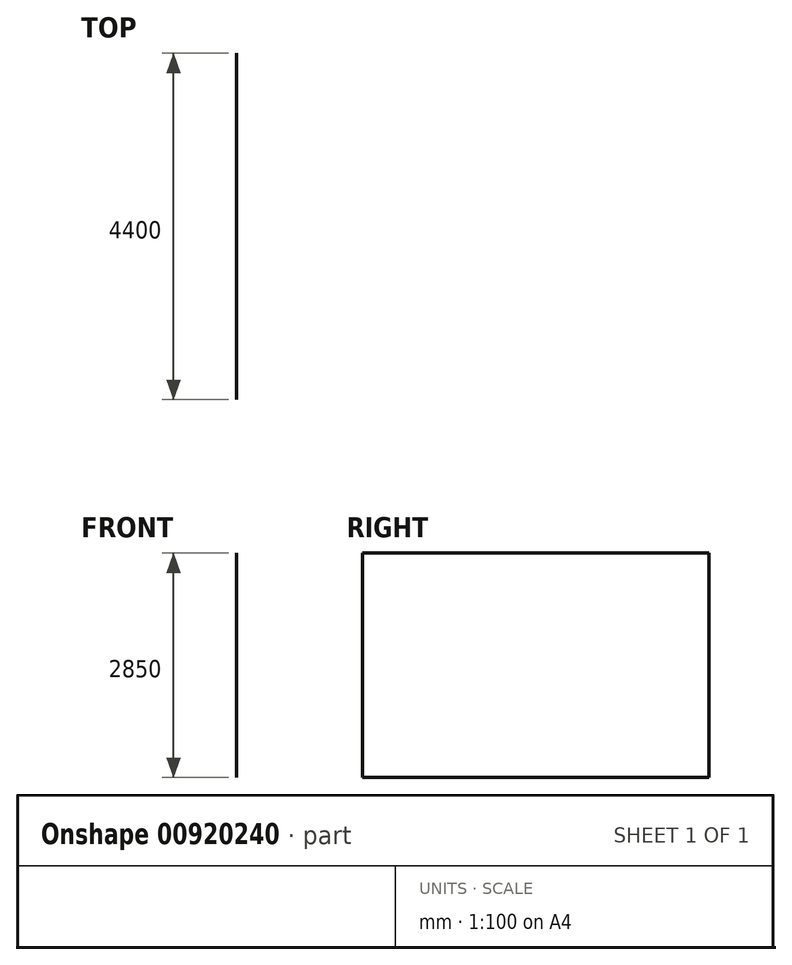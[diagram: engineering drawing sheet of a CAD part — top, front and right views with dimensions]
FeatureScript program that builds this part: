
annotation { "Feature Type Name" : "Feature", "Feature Type Description" : "" }
export const myFeature = defineFeature(function(context is Context, id is Id, definition is map)
    precondition{}
    {
        {
            var Q0;
            Q0=qCreatedBy(makeId("Right.planeOp"),FACE);
            var sketch = newSketch(context, id + "F0", { "sketchPlane" : qUnion([Q0])});
            skLineSegment(sketch, "E0", {"start": v(0, 0) * mm, "end": v(0, 2850) * mm});
            skLineSegment(sketch, "E1", {"start": v(0, 2850) * mm, "end": v(2200, 2850) * mm});
            skLineSegment(sketch, "E2", {"start": v(2200, 0) * mm, "end": v(2200, 2850) * mm});
            skLineSegment(sketch, "E3", {"start": v(2200, 2850) * mm, "end": v(4400, 2850) * mm});
            skLineSegment(sketch, "E4", {"start": v(4400, 2850) * mm, "end": v(4400, 0) * mm});
            skLineSegment(sketch, "E5", {"start": v(4400, 2850) * mm, "end": v(5400, 2850) * mm});
            skPoint(sketch, "E6", {"position": v(4900, 2850) * mm});
            skPoint(sketch, "E7", {"position": v(3300, 2850) * mm});
            skPoint(sketch, "E8", {"position": v(1100, 2850) * mm});
            skPoint(sketch, "E9", {"position": v(1650, 2850) * mm});
            skPoint(sketch, "E10", {"position": v(550, 2850) * mm});
            skPoint(sketch, "E11", {"position": v(2750, 2850) * mm});
            skPoint(sketch, "E12", {"position": v(3850, 2850) * mm});
            skLineSegment(sketch, "E13", {"start": v(0, 0) * mm, "end": v(2200, 0) * mm, "construction": true});
            skLineSegment(sketch, "E14", {"start": v(2200, 0) * mm, "end": v(4400, 0) * mm, "construction": true});
            skSolve(sketch);
        }
        {
            var Q0;
            Q0=qCreatedBy(makeId("Right.planeOp"),FACE);
            cPlane(context, id + "F1", {"entities" : qUnion([Q0]), "cplaneType" : CPlaneType.OFFSET, "offset" : 5250 * mm, "width" : 150 * mm, "height" : 150 * mm});
        }
        {
            var Q0;
            Q0=qCreatedBy(id+"F1.planeOp",FACE);
            var sketch = newSketch(context, id + "F2", { "sketchPlane" : qUnion([Q0])});
            skLineSegment(sketch, "E15.0", {"start": v(0, 0) * mm, "end": v(0, 2850) * mm});
            skLineSegment(sketch, "E16.0", {"start": v(0, 2850) * mm, "end": v(2200, 2850) * mm});
            skPoint(sketch, "E17.0", {"position": v(550, 2850) * mm});
            skPoint(sketch, "E18.0", {"position": v(1100, 2850) * mm});
            skPoint(sketch, "E19.0", {"position": v(1650, 2850) * mm});
            skPoint(sketch, "E20.0", {"position": v(2200, 2850) * mm});
            skLineSegment(sketch, "E21.0", {"start": v(2200, 0) * mm, "end": v(2200, 2850) * mm});
            skLineSegment(sketch, "E22.0", {"start": v(2200, 2850) * mm, "end": v(4400, 2850) * mm});
            skPoint(sketch, "E23.0", {"position": v(2750, 2850) * mm});
            skPoint(sketch, "E24.0", {"position": v(3300, 2850) * mm});
            skPoint(sketch, "E25.0", {"position": v(3850, 2850) * mm});
            skPoint(sketch, "E26.0", {"position": v(4400, 2850) * mm});
            skLineSegment(sketch, "E27.0", {"start": v(4400, 2850) * mm, "end": v(4400, 0) * mm});
            skLineSegment(sketch, "E28.0", {"start": v(4400, 2850) * mm, "end": v(5400, 2850) * mm});
            skPoint(sketch, "E29.0", {"position": v(4900, 2850) * mm});
            skPoint(sketch, "E30.0", {"position": v(0, 2850) * mm});
            skPoint(sketch, "E31.0", {"position": v(5400, 2850) * mm});
            skLineSegment(sketch, "E32", {"start": v(0, 0) * mm, "end": v(2200, 0) * mm, "construction": true});
            skLineSegment(sketch, "E33", {"start": v(2200, 0) * mm, "end": v(4400, 0) * mm, "construction": true});
            skSolve(sketch);
        }
        {
            var Q0;
            Q0=sQuery(id+"F0.wireOp",VERTEX,"E0.end");
            var Q1;
            Q1=sQuery(id+"F2.wireOp",VERTEX,"E30.0");
            var Q2;
            Q2=sQuery(id+"F2.wireOp",VERTEX,"E20.0");
            cPlane(context, id + "F3", {"entities" : qUnion([Q0, Q1, Q2]), "cplaneType" : CPlaneType.THREE_POINT, "offset" : 25 * mm, "width" : 150 * mm, "height" : 150 * mm});
        }
        {
            var Q0;
            Q0=sQuery(id+"F0.wireOp",EDGE,"E4");
            var Q1;
            Q1=sQuery(id+"F0.wireOp",EDGE,"E2");
            loft(context, id + "F4", {"bodyType" : ToolBodyType.SURFACE, "wireProfilesArray" : [{ "wireProfileEntities" : qUnion([Q0]) }, { "wireProfileEntities" : qUnion([Q1]) }]});
        }
        {
            var Q0;
            Q0=sQuery(id+"F0.wireOp",EDGE,"E0");
            var Q1;
            Q1=sQuery(id+"F0.wireOp",EDGE,"E2");
            loft(context, id + "F5", {"bodyType" : ToolBodyType.SURFACE, "surfaceOperationType" : NewSurfaceOperationType.ADD, "wireProfilesArray" : [{ "wireProfileEntities" : qUnion([Q0]) }, { "wireProfileEntities" : qUnion([Q1]) }]});
        }
    });
